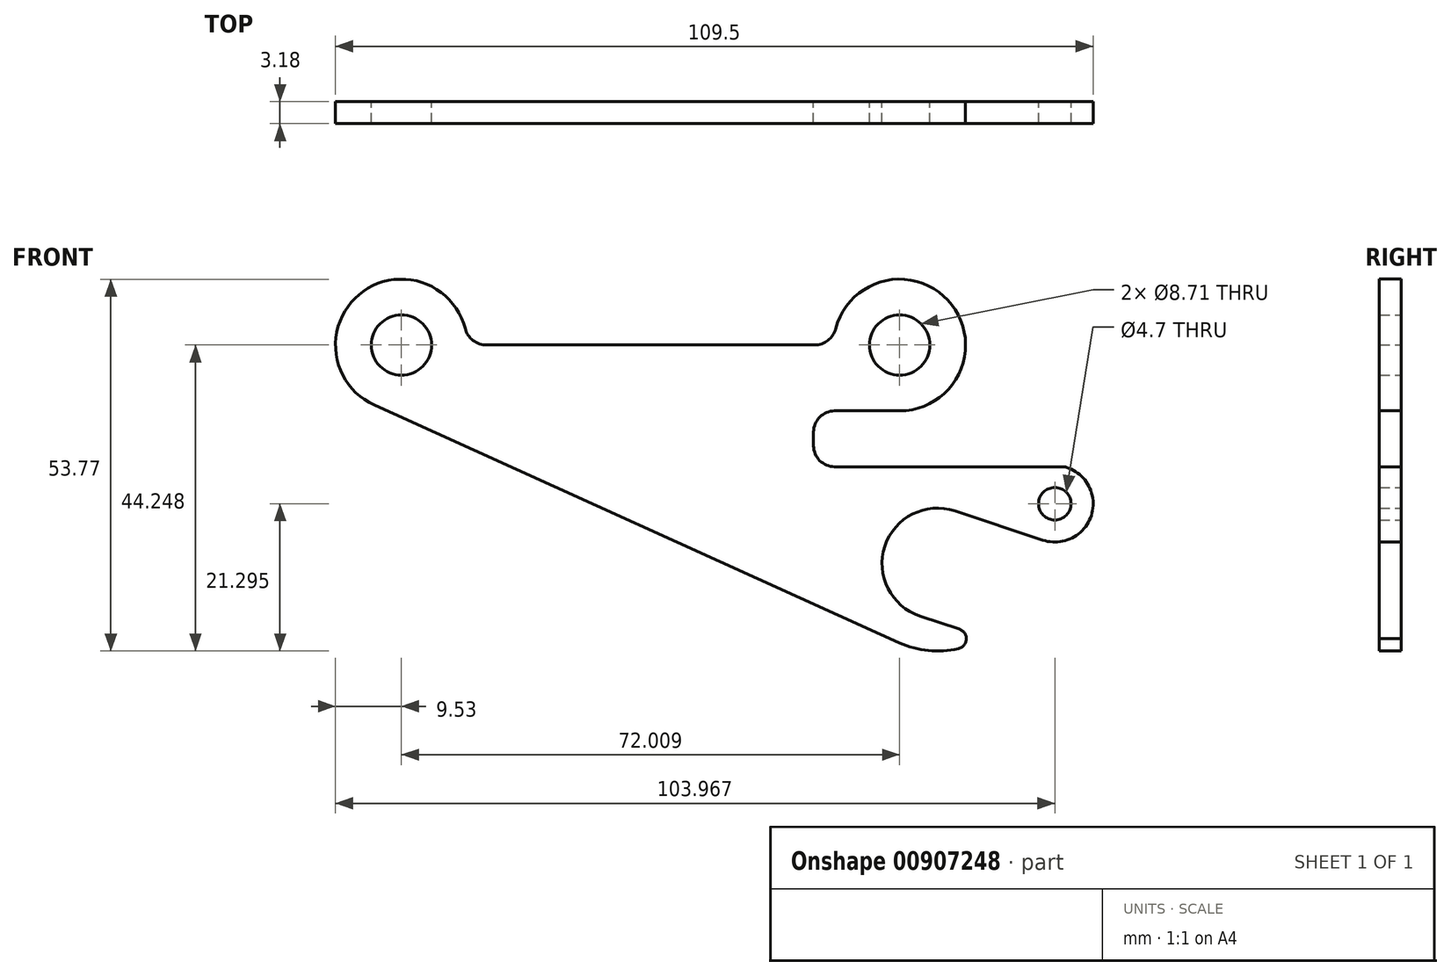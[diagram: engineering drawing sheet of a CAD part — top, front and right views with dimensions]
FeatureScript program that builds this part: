
annotation { "Feature Type Name" : "Feature", "Feature Type Description" : "" }
export const myFeature = defineFeature(function(context is Context, id is Id, definition is map)
    precondition{}
    {
        {
            var Q0;
            Q0=qCreatedBy(makeId("Front.planeOp"),FACE);
            var sketch = newSketch(context, id + "F0", { "sketchPlane" : qUnion([Q0])});
            skCircle(sketch, "E0", {"center": v(0, 0) * mm, "radius": 8 * mm, "construction": true});
            skLineSegment(sketch, "E1", {"start": v(0, 46.45) * mm, "end": v(0, -50.14) * mm, "construction": true});
            skLineSegment(sketch, "E2", {"start": v(-42.55, 0) * mm, "end": v(50.18, 0) * mm, "construction": true});
            skLineSegment(sketch, "E3", {"start": v(0, 0) * mm, "end": v(49.93, 25.44) * mm, "construction": true});
            skLineSegment(sketch, "E4", {"start": v(16.97, 45.23) * mm, "end": v(16.97, -46.08) * mm, "construction": true});
            skCircle(sketch, "E5", {"center": v(16.97, 8.65) * mm, "radius": 5.54 * mm, "construction": true});
            skCircle(sketch, "E6", {"center": v(16.97, 8.65) * mm, "radius": 2.35 * mm});
            skLineSegment(sketch, "E7", {"start": v(-5.46, 42.26) * mm, "end": v(-5.46, -34.76) * mm, "construction": true});
            skLineSegment(sketch, "E8", {"start": v(-100.04, 31.6) * mm, "end": v(46, 31.6) * mm, "construction": true});
            skCircle(sketch, "E9", {"center": v(-5.46, 31.6) * mm, "radius": 9.53 * mm, "construction": true});
            skCircle(sketch, "E10", {"center": v(-5.46, 31.6) * mm, "radius": 4.36 * mm});
            skLineSegment(sketch, "E11", {"start": v(-77.47, 46.74) * mm, "end": v(-77.47, -30.68) * mm, "construction": true});
            skCircle(sketch, "E12", {"center": v(-77.47, 31.6) * mm, "radius": 9.53 * mm, "construction": true});
            skCircle(sketch, "E13", {"center": v(-77.47, 31.6) * mm, "radius": 4.36 * mm});
            skCircle(sketch, "E14", {"center": v(0, 0) * mm, "radius": 12.7 * mm, "construction": true});
            skLineSegment(sketch, "E15", {"start": v(4.2, 24.34) * mm, "end": v(4.2, -29.25) * mm, "construction": true});
            skLineSegment(sketch, "E16", {"start": v(-77.47, 41.12) * mm, "end": v(-5.46, 41.12) * mm, "construction": true});
            skLineSegment(sketch, "E17", {"start": v(-104.49, -12.75) * mm, "end": v(51, -12.75) * mm, "construction": true});
            skLineSegment(sketch, "E18", {"start": v(-17.9, 28.64) * mm, "end": v(-17.9, 1.87) * mm, "construction": true});
            skLineSegment(sketch, "E19", {"start": v(-41.8, 22.07) * mm, "end": v(9.84, 22.07) * mm, "construction": true});
            skLineSegment(sketch, "E20", {"start": v(-41.03, 14) * mm, "end": v(24.47, 14) * mm, "construction": true});
            skLineSegment(sketch, "E21", {"start": v(-17.9, 22.07) * mm, "end": v(-17.9, 14) * mm});
            skPoint(sketch, "E21.endSnap0", {"position": v(-17.9, 15.26) * mm});
            skLineSegment(sketch, "E22", {"start": v(-81.4, 22.92) * mm, "end": v(-5.46, -11.47) * mm});
            skArc(sketch, "E23", {"start": v(-77.47, 41.12) * mm, "mid": v(-86.78, 33.6) * mm, "end": v(-81.4, 22.92) * mm});
            skArc(sketch, "E24", {"start": v(-67.95, 31.6) * mm, "mid": v(-70.73, 38.33) * mm, "end": v(-77.47, 41.12) * mm});
            skLineSegment(sketch, "E25", {"start": v(-67.95, 31.6) * mm, "end": v(-14.99, 31.6) * mm});
            skArc(sketch, "E26", {"start": v(-5.46, 41.12) * mm, "mid": v(-12.2, 38.33) * mm, "end": v(-14.99, 31.6) * mm});
            skArc(sketch, "E27", {"start": v(-5.46, 22.07) * mm, "mid": v(4.06, 31.6) * mm, "end": v(-5.46, 41.12) * mm});
            skLineSegment(sketch, "E28", {"start": v(-5.46, 22.07) * mm, "end": v(-17.9, 22.07) * mm});
            skLineSegment(sketch, "E29", {"start": v(-17.9, 14) * mm, "end": v(18.4, 14) * mm});
            skLineSegment(sketch, "E30", {"start": v(2.51, 7.6) * mm, "end": v(15.23, 3.39) * mm, "construction": true});
            skLineSegment(sketch, "E31", {"start": v(-2.51, -7.6) * mm, "end": v(15.98, -13.72) * mm, "construction": true});
            skPoint(sketch, "E32", {"position": v(4.2, -9.81) * mm});
            skPoint(sketch, "E33", {"position": v(4.2, -11.99) * mm});
            skArc(sketch, "E34", {"start": v(-5.46, -11.47) * mm, "mid": v(-0.68, -12.64) * mm, "end": v(4.2, -11.99) * mm});
            skArc(sketch, "E35", {"start": v(2.51, 7.6) * mm, "mid": v(-7.6, 2.51) * mm, "end": v(-2.51, -7.6) * mm});
            skLineSegment(sketch, "E36", {"start": v(-2.51, -7.6) * mm, "end": v(4.2, -9.81) * mm});
            skLineSegment(sketch, "E37", {"start": v(4.2, -9.81) * mm, "end": v(4.2, -11.99) * mm});
            skLineSegment(sketch, "E38", {"start": v(2.51, 7.6) * mm, "end": v(15.23, 3.39) * mm});
            skArc(sketch, "E39", {"start": v(15.23, 3.39) * mm, "mid": v(22.27, 7.06) * mm, "end": v(18.4, 14) * mm});
            skSolve(sketch);
        }
        {
            var Q0;
            Q0=makeQuery(id+"F0.imprint","IMPRINT",FACE,{"disambiguationData":[TD([[makeQuery(id+"F0.imprint","IMPRINT",EDGE,{"derivedFrom":sQuery(id+"F0.wireOp",EDGE,"E6")}),-1.0]])]});
            extrude(context, id + "F1", {"entities" : qUnion([Q0]), "depth" : 3.17 * mm, "offsetDistance" : 25.4 * mm});
        }
        {
            var Q0;
            Q0=makeQuery(id+"F1.opExtrude","SWEPT_EDGE",EDGE,{"disambiguationData":[OSD([sQuery(id+"F0.wireOp",EDGE,"E36"),sQuery(id+"F0.wireOp",EDGE,"E37")])]});
            var Q1;
            Q1=makeQuery(id+"F1.opExtrude","SWEPT_EDGE",EDGE,{"disambiguationData":[OSD([sQuery(id+"F0.wireOp",EDGE,"E34"),sQuery(id+"F0.wireOp",EDGE,"E37")])]});
            fillet(context, id + "F2", {"entities" : qUnion([Q0, Q1]), "radius" : 1.52 * mm, "tangentPropagation" : true, "allowEdgeOverflow" : false});
        }
        {
            var Q0;
            Q0=makeQuery(id+"F1.opExtrude","SWEPT_EDGE",EDGE,{"disambiguationData":[OSD([sQuery(id+"F0.wireOp",EDGE,"E21"),sQuery(id+"F0.wireOp",EDGE,"E28")])]});
            var Q1;
            Q1=makeQuery(id+"F1.opExtrude","SWEPT_EDGE",EDGE,{"disambiguationData":[OSD([sQuery(id+"F0.wireOp",EDGE,"E21"),sQuery(id+"F0.wireOp",EDGE,"E29")])]});
            fillet(context, id + "F3", {"entities" : qUnion([Q0, Q1]), "radius" : 3.05 * mm, "tangentPropagation" : true, "allowEdgeOverflow" : false});
        }
        {
            var Q0;
            Q0=makeQuery(id+"F1.opExtrude","SWEPT_EDGE",EDGE,{"disambiguationData":[OSD([sQuery(id+"F0.wireOp",EDGE,"E24"),sQuery(id+"F0.wireOp",EDGE,"E25")])]});
            var Q1;
            Q1=makeQuery(id+"F1.opExtrude","SWEPT_EDGE",EDGE,{"disambiguationData":[OSD([sQuery(id+"F0.wireOp",EDGE,"E25"),sQuery(id+"F0.wireOp",EDGE,"E26")])]});
            fillet(context, id + "F4", {"entities" : qUnion([Q0, Q1]), "radius" : 3.17 * mm, "tangentPropagation" : true, "allowEdgeOverflow" : false});
        }
        {
            var Q0;
            Q0=makeQuery(id+"F1.opExtrude","SWEPT_EDGE",EDGE,{"disambiguationData":[OSD([sQuery(id+"F0.wireOp",EDGE,"E29"),sQuery(id+"F0.wireOp",EDGE,"E39")])]});
            fillet(context, id + "F5", {"entities" : qUnion([Q0]), "radius" : 1.52 * mm, "tangentPropagation" : true, "allowEdgeOverflow" : false});
        }
    });
